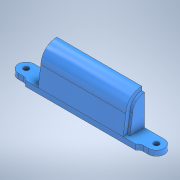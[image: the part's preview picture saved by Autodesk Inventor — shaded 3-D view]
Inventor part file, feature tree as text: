
AUTODESK INVENTOR PART (.ipt)
format: ipt  version: 2022 (Build 260153000, 153)  size: 224,768 bytes
history: native  units: mm
features: extrude x4, sketch x4, mirror x1
ambient origin geometry x8: Origin, YZ Plane, XZ Plane, XY Plane, X Axis, Y Axis, Z Axis, Center Point
bodies: Solid1 (feature_tree)
feature tree (9):
  extrude  "Extrusion1"  Depth=6.0mm
  extrude  "Extrusion2"  Depth=2.0mm
  extrude  "Extrusion3"  Depth=3.0mm
  extrude  "Extrusion4"  Depth=3.0mm
  mirror  "Mirror1"
  sketch  "Sketch1"  dims[d0=24.5mm d1=6.0mm]
  sketch  "Sketch2"  dims[d2=2.0mm d3=2.0mm]
  sketch  "Sketch3"  dims[d4=3.0mm d5=3.0mm]
  sketch  "Sketch4"  dims[d6=9.0mm d7=3.0mm d8=18.0mm d9=4.0mm d10=4.0mm d11=2.0mm d12=2.0mm d13=0.0mm d14=10.0mm d15=0.0mm d16=7.0mm d17=3.0mm d18=16.0mm d19=0.0mm d20=6.0mm d21=3.0mm d22=7.0mm d23=4.0mm d24=9.0mm d25=1.5mm d26=1.0mm d27=1.0mm d28=0.0mm d29=0.0mm d30=0.0mm d31=0.0mm]
